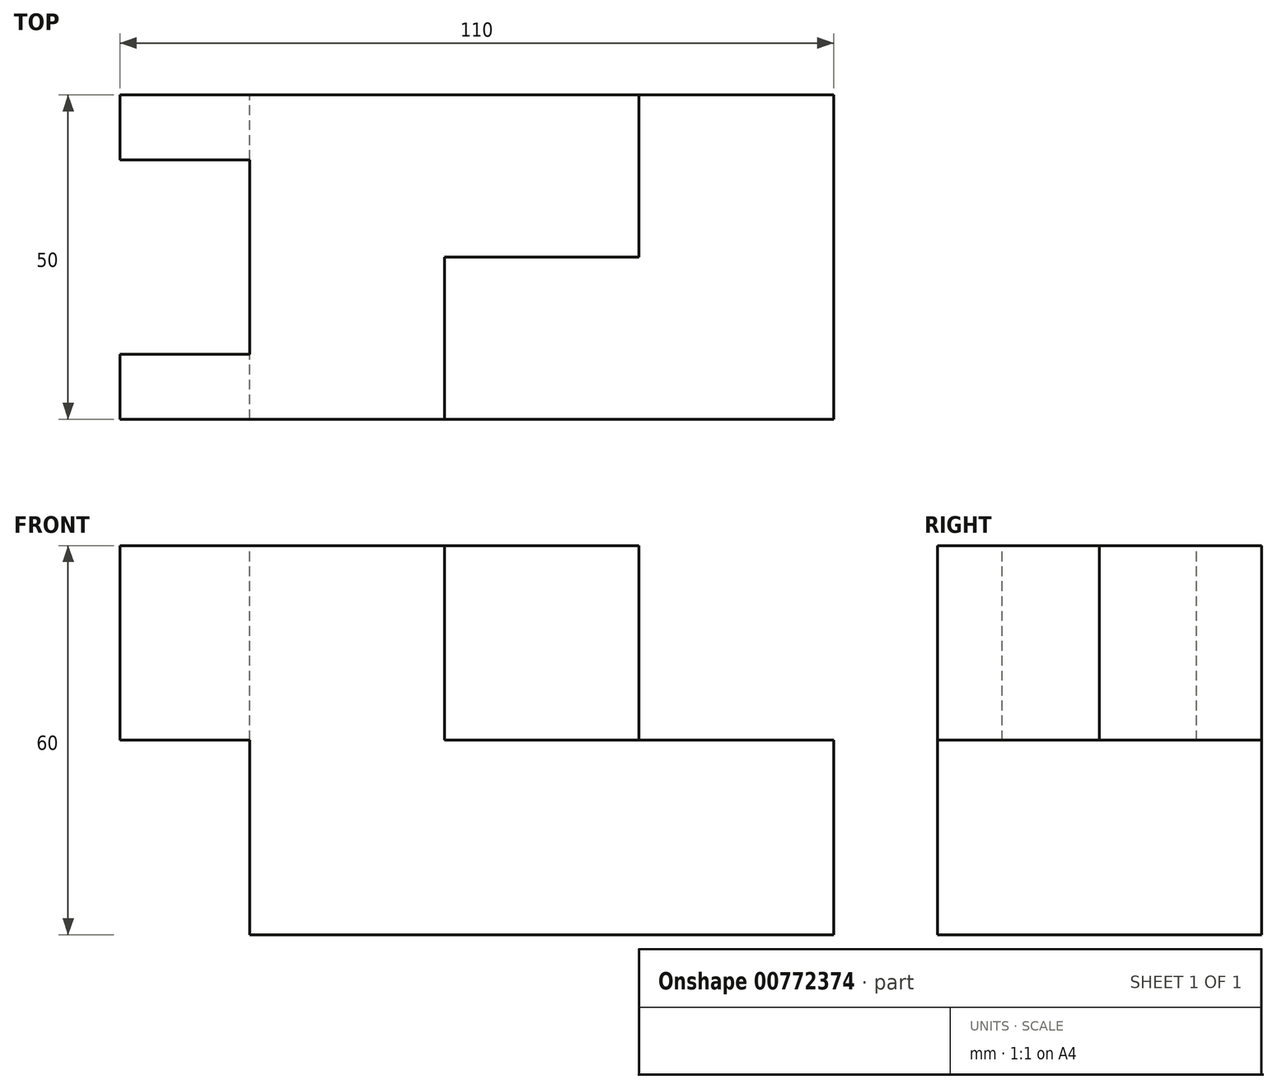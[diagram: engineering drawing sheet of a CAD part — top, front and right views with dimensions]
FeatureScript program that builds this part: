
annotation { "Feature Type Name" : "Feature", "Feature Type Description" : "" }
export const myFeature = defineFeature(function(context is Context, id is Id, definition is map)
    precondition{}
    {
        {
            var Q0;
            Q0=qCreatedBy(makeId("Top.planeOp"),FACE);
            var sketch = newSketch(context, id + "F0", { "sketchPlane" : qUnion([Q0])});
            skLineSegment(sketch, "E0", {"start": v(0, 0) * mm, "end": v(0, 10) * mm});
            skLineSegment(sketch, "E1", {"start": v(0, 10) * mm, "end": v(20, 10) * mm});
            skLineSegment(sketch, "E2", {"start": v(20, 10) * mm, "end": v(20, 40) * mm});
            skLineSegment(sketch, "E3", {"start": v(20, 40) * mm, "end": v(0, 40) * mm});
            skLineSegment(sketch, "E4", {"start": v(0, 40) * mm, "end": v(0, 50) * mm});
            skLineSegment(sketch, "E5", {"start": v(0, 50) * mm, "end": v(80, 50) * mm});
            skLineSegment(sketch, "E6", {"start": v(80, 50) * mm, "end": v(80, 25) * mm});
            skLineSegment(sketch, "E7", {"start": v(80, 25) * mm, "end": v(50, 25) * mm});
            skLineSegment(sketch, "E8", {"start": v(50, 25) * mm, "end": v(50, 0) * mm});
            skLineSegment(sketch, "E9", {"start": v(50, 0) * mm, "end": v(0, 0) * mm});
            skLineSegment(sketch, "E10", {"start": v(50, 0) * mm, "end": v(110, 0) * mm});
            skLineSegment(sketch, "E11", {"start": v(110, 0) * mm, "end": v(110, 50) * mm});
            skLineSegment(sketch, "E12", {"start": v(110, 50) * mm, "end": v(80, 50) * mm});
            skLineSegment(sketch, "E13", {"start": v(20, 10) * mm, "end": v(20, 0) * mm});
            skLineSegment(sketch, "E14", {"start": v(20, 40) * mm, "end": v(20, 50) * mm});
            skLineSegment(sketch, "E15", {"start": v(80, 25) * mm, "end": v(80, 0) * mm});
            skLineSegment(sketch, "E16", {"start": v(50, 25) * mm, "end": v(50, 50) * mm});
            skSolve(sketch);
        }
        {
            var Q0;
            Q0=makeQuery(id+"F0.imprint","IMPRINT",FACE,{"disambiguationData":[TD([[makeQuery(id+"F0.imprint","IMPRINT",EDGE,{"derivedFrom":sQuery(id+"F0.wireOp",EDGE,"E0")}),-1.0]])]});
            var Q1;
            Q1=makeQuery(id+"F0.imprint","IMPRINT",FACE,{"disambiguationData":[TD([[makeQuery(id+"F0.imprint","IMPRINT",EDGE,{"derivedFrom":sQuery(id+"F0.wireOp",EDGE,"E3")}),-1.0]])]});
            var Q2;
            Q2=makeQuery(id+"F0.imprint","IMPRINT",FACE,{"disambiguationData":[TD([[makeQuery(id+"F0.imprint","IMPRINT",EDGE,{"derivedFrom":sQuery(id+"F0.wireOp",EDGE,"E2")}),-1.0]])]});
            var Q3;
            {var subQ0=sQuery(id+"F0.wireOp",EDGE,"E6");Q3=makeQuery(id+"F0.imprint","IMPRINT",FACE,{"disambiguationData":[TD([[makeQuery(id+"F0.imprint","IMPRINT",EDGE,{"derivedFrom":subQ0}),-1.0]])]});}
            extrude(context, id + "F1", {"entities" : qUnion([Q0, Q1, Q2, Q3]), "oppositeDirection" : true, "depth" : 30 * mm, "offsetDistance" : 25 * mm});
        }
        {
            var Q0;
            Q0=makeQuery(id+"F0.imprint","IMPRINT",FACE,{"disambiguationData":[TD([[makeQuery(id+"F0.imprint","IMPRINT",EDGE,{"derivedFrom":sQuery(id+"F0.wireOp",EDGE,"E2")}),-1.0]])]});
            var Q1;
            {var subQ0=sQuery(id+"F0.wireOp",EDGE,"E6");Q1=makeQuery(id+"F0.imprint","IMPRINT",FACE,{"disambiguationData":[TD([[makeQuery(id+"F0.imprint","IMPRINT",EDGE,{"derivedFrom":subQ0}),-1.0]])]});}
            var Q2;
            Q2=makeQuery(id+"F0.imprint","IMPRINT",FACE,{"disambiguationData":[TD([[makeQuery(id+"F0.imprint","IMPRINT",EDGE,{"derivedFrom":sQuery(id+"F0.wireOp",EDGE,"E6")}),1.0]])]});
            var Q3;
            Q3=makeQuery(id+"F0.imprint","IMPRINT",FACE,{"disambiguationData":[TD([[makeQuery(id+"F0.imprint","IMPRINT",EDGE,{"derivedFrom":sQuery(id+"F0.wireOp",EDGE,"E7")}),1.0]])]});
            extrude(context, id + "F2", {"entities" : qUnion([Q0, Q1, Q2, Q3]), "operationType" : NewBodyOperationType.ADD, "oppositeDirection" : true, "depth" : 60 * mm, "offsetDistance" : 25 * mm, "hasSecondDirection" : true, "secondDirectionOppositeDirection" : true, "secondDirectionDepth" : 30 * mm});
        }
    });
